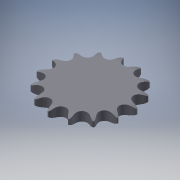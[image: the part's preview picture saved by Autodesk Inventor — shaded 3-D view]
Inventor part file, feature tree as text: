
AUTODESK INVENTOR PART (.ipt)
format: ipt  version: 2016 (Build 200138000, 138)  size: 484,864 bytes
history: native  units: mm
features: other x6, extrude x2, pattern_linear x1, pattern_circular x1
ambient origin geometry x8: Origin, YZ Plane, XZ Plane, XY Plane, X Axis, Y Axis, Z Axis, Center Point
bodies: Solid1 (feature_tree)
feature tree (10):
  other  "Theoretical Tooth Profile"
  other  "Tooth Profile"
  other  "Section Profile"
  other  "Shroud"
  other  "Strand"
  pattern_linear  "Strand Pattern"  Spacing1=61.083626mm  [1 undecoded]
  extrude  "Theoretical Tooth"  Depth=4.18879mm
  extrude  "Tooth"  Depth=4.29755mm
  pattern_circular  "Tooth Pattern"  [2 undecoded]
  other  "Timing Plane"
note: 3 required parameter values undecoded (feature->parameter linkage not recoverable at this tier; creation-order binding heuristic only, values carry confidence <= 0.55)
